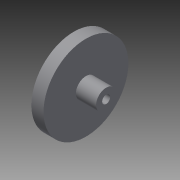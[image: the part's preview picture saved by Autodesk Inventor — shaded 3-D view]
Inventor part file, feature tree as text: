
AUTODESK INVENTOR PART (.ipt)
format: ipt  version: 2013 (Build 170138000, 138)  size: 84,992 bytes
history: native  units: mm
features: extrude x2, sketch x2, other x1
ambient origin geometry x8: Origin, YZ Plane, XZ Plane, XY Plane, X Axis, Y Axis, Z Axis, Center Point
feature tree (5):
  other  "ソリッド1"
  extrude  "押し出し1"  Depth=2.0mm
  extrude  "押し出し2"  Depth=5.0mm
  sketch  "スケッチ1"
  sketch  "スケッチ2"
